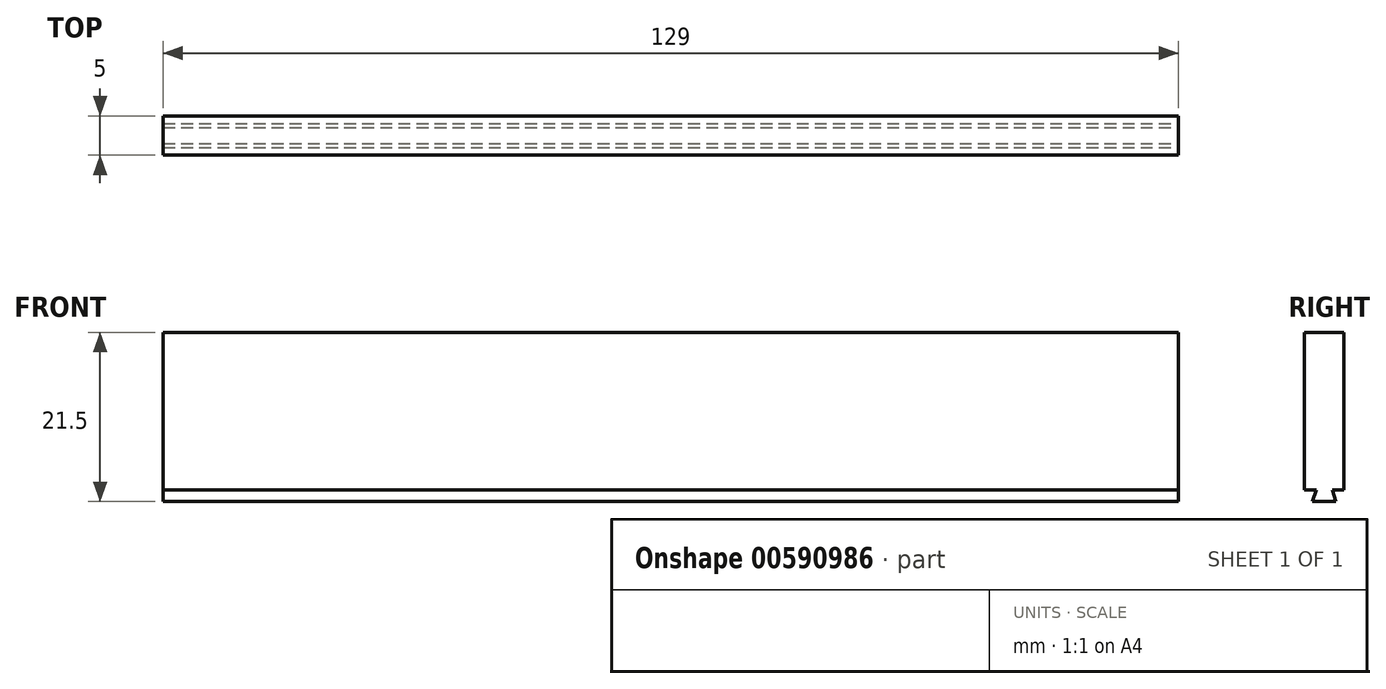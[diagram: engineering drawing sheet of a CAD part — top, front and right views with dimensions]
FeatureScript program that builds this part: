
annotation { "Feature Type Name" : "Feature", "Feature Type Description" : "" }
export const myFeature = defineFeature(function(context is Context, id is Id, definition is map)
    precondition{}
    {
        {
            var Q0;
            Q0=qCreatedBy(makeId("Front.planeOp"),FACE);
            var sketch = newSketch(context, id + "F0", { "sketchPlane" : qUnion([Q0])});
            skLineSegment(sketch, "E0.bottom", {"start": v(64.5, 10.75) * mm, "end": v(-64.5, 10.75) * mm});
            skLineSegment(sketch, "E0.top", {"start": v(64.5, -10.75) * mm, "end": v(-64.5, -10.75) * mm});
            skLineSegment(sketch, "E0.left", {"start": v(64.5, 10.75) * mm, "end": v(64.5, -10.75) * mm});
            skLineSegment(sketch, "E0.right", {"start": v(-64.5, 10.75) * mm, "end": v(-64.5, -10.75) * mm});
            skPoint(sketch, "E0.middle", {"position": v(0, 0) * mm});
            skSolve(sketch);
        }
        {
            var Q0;
            Q0=makeQuery(id+"F0.imprint","IMPRINT",FACE,{"disambiguationData":[TD([[makeQuery(id+"F0.imprint","IMPRINT",EDGE,{"derivedFrom":sQuery(id+"F0.wireOp",EDGE,"E0.bottom")}),1.0]])]});
            extrude(context, id + "F1", {"entities" : qUnion([Q0]), "depth" : 5 * mm, "offsetDistance" : 25 * mm});
        }
        {
            var Q0;
            Q0=makeQuery(id+"F1.opExtrude","SWEPT_FACE",FACE,{"disambiguationData":[OSD([sQuery(id+"F0.wireOp",EDGE,"E0.left")])]});
            var sketch = newSketch(context, id + "F2", { "sketchPlane" : qUnion([Q0])});
            skLineSegment(sketch, "E1", {"start": v(-3.5, -9.25) * mm, "end": v(-4, -10.75) * mm});
            skLineSegment(sketch, "E2", {"start": v(-1, -10.75) * mm, "end": v(-1.5, -9.25) * mm});
            skLineSegment(sketch, "E3", {"start": v(-3.5, -9.25) * mm, "end": v(-5, -9.25) * mm});
            skLineSegment(sketch, "E4", {"start": v(-5, -9.25) * mm, "end": v(-5, -10.75) * mm});
            skLineSegment(sketch, "E5", {"start": v(-5, -10.75) * mm, "end": v(-4, -10.75) * mm});
            skLineSegment(sketch, "E6", {"start": v(-1.5, -9.25) * mm, "end": v(0, -9.25) * mm});
            skLineSegment(sketch, "E7", {"start": v(0, -9.25) * mm, "end": v(0, -10.75) * mm});
            skLineSegment(sketch, "E8", {"start": v(0, -10.75) * mm, "end": v(-1, -10.75) * mm});
            skSolve(sketch);
        }
        {
            var Q0;
            Q0=makeQuery(id+"F2.imprint","IMPRINT",FACE,{"disambiguationData":[TD([[makeQuery(id+"F2.imprint","IMPRINT",EDGE,{"derivedFrom":sQuery(id+"F2.wireOp",EDGE,"E1")}),-1.0]])]});
            var Q1;
            Q1=makeQuery(id+"F2.imprint","IMPRINT",FACE,{"disambiguationData":[TD([[makeQuery(id+"F2.imprint","IMPRINT",EDGE,{"derivedFrom":sQuery(id+"F2.wireOp",EDGE,"E2")}),-1.0]])]});
            extrude(context, id + "F3", {"entities" : qUnion([Q0, Q1]), "operationType" : NewBodyOperationType.REMOVE, "endBound" : BoundingType.THROUGH_ALL, "oppositeDirection" : true, "depth" : 25 * mm, "offsetDistance" : 25 * mm});
        }
    });
